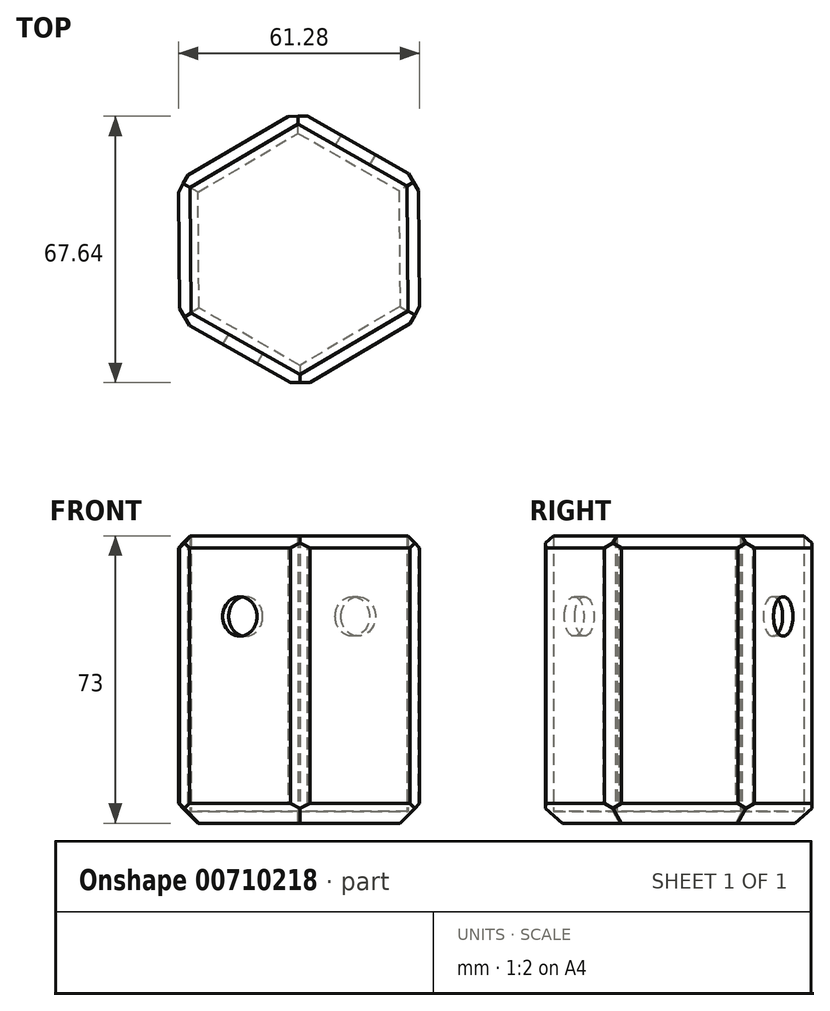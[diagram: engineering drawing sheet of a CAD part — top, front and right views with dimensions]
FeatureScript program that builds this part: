
annotation { "Feature Type Name" : "Feature", "Feature Type Description" : "" }
export const myFeature = defineFeature(function(context is Context, id is Id, definition is map)
    precondition{}
    {
        {
            var Q0;
            Q0=qCreatedBy(makeId("Top.planeOp"),FACE);
            var sketch = newSketch(context, id + "F0", { "sketchPlane" : qUnion([Q0])});
            skCircle(sketch, "E0.cCircle", {"center": v(0, 0) * mm, "radius": 30.52 * mm, "construction": true});
            skLineSegment(sketch, "E0.0", {"start": v(-30.67, 17.36) * mm, "end": v(-0.3, 35.24) * mm});
            skLineSegment(sketch, "E0.1", {"start": v(-0.3, 35.24) * mm, "end": v(30.37, 17.88) * mm});
            skLineSegment(sketch, "E0.2", {"start": v(30.37, 17.88) * mm, "end": v(30.67, -17.36) * mm});
            skLineSegment(sketch, "E0.3", {"start": v(30.67, -17.36) * mm, "end": v(0.3, -35.24) * mm});
            skLineSegment(sketch, "E0.4", {"start": v(0.3, -35.24) * mm, "end": v(-30.37, -17.88) * mm});
            skLineSegment(sketch, "E0.5", {"start": v(-30.37, -17.88) * mm, "end": v(-30.67, 17.36) * mm});
            skPoint(sketch, "E0.0.midPoint", {"position": v(-15.48, 26.3) * mm});
            skSolve(sketch);
        }
        {
            var Q0;
            Q0=makeQuery(id+"F0.imprint","IMPRINT",FACE,{"disambiguationData":[TD([[makeQuery(id+"F0.imprint","IMPRINT",EDGE,{"derivedFrom":sQuery(id+"F0.wireOp",EDGE,"E0.0")}),-1.0]])]});
            extrude(context, id + "F1", {"entities" : qUnion([Q0]), "depth" : 75 * mm, "offsetDistance" : 25 * mm});
        }
        {
            var Q0;
            Q0=makeQuery(id+"F1.opExtrude","CAP_FACE",FACE,{"disambiguationData":[OSD([sQuery(id+"F0.wireOp",EDGE,"E0.0"),sQuery(id+"F0.wireOp",EDGE,"E0.1"),sQuery(id+"F0.wireOp",EDGE,"E0.2"),sQuery(id+"F0.wireOp",EDGE,"E0.3"),sQuery(id+"F0.wireOp",EDGE,"E0.4"),sQuery(id+"F0.wireOp",EDGE,"E0.5")])],"isStart":false});
            shell(context, id + "F2", {"entities" : qUnion([Q0]), "thickness" : 3 * mm});
        }
        {
            var Q0;
            Q0=makeQuery(id+"F1.opExtrude","CAP_FACE",FACE,{"disambiguationData":[OSD([sQuery(id+"F0.wireOp",EDGE,"E0.0"),sQuery(id+"F0.wireOp",EDGE,"E0.1"),sQuery(id+"F0.wireOp",EDGE,"E0.2"),sQuery(id+"F0.wireOp",EDGE,"E0.3"),sQuery(id+"F0.wireOp",EDGE,"E0.4"),sQuery(id+"F0.wireOp",EDGE,"E0.5")])],"isStart":true});
            chamfer(context, id + "F3", {"entities" : qUnion([Q0]), "width" : 5 * mm, "tangentPropagation" : true});
        }
        {
            var Q0;
            Q0=makeQuery(id+"F1.opExtrude","CAP_EDGE",EDGE,{"disambiguationData":[OSD([sQuery(id+"F0.wireOp",EDGE,"E0.4")])],"isStart":false});
            var Q1;
            Q1=makeQuery(id+"F1.opExtrude","CAP_EDGE",EDGE,{"disambiguationData":[OSD([sQuery(id+"F0.wireOp",EDGE,"E0.5")])],"isStart":false});
            var Q2;
            Q2=makeQuery(id+"F1.opExtrude","CAP_EDGE",EDGE,{"disambiguationData":[OSD([sQuery(id+"F0.wireOp",EDGE,"E0.0")])],"isStart":false});
            var Q3;
            Q3=makeQuery(id+"F1.opExtrude","CAP_EDGE",EDGE,{"disambiguationData":[OSD([sQuery(id+"F0.wireOp",EDGE,"E0.1")])],"isStart":false});
            var Q4;
            Q4=makeQuery(id+"F1.opExtrude","CAP_EDGE",EDGE,{"disambiguationData":[OSD([sQuery(id+"F0.wireOp",EDGE,"E0.2")])],"isStart":false});
            var Q5;
            Q5=makeQuery(id+"F1.opExtrude","CAP_EDGE",EDGE,{"disambiguationData":[OSD([sQuery(id+"F0.wireOp",EDGE,"E0.3")])],"isStart":false});
            chamfer(context, id + "F4", {"entities" : qUnion([Q0, Q1, Q2, Q3, Q4, Q5]), "width" : 5 * mm, "tangentPropagation" : true});
        }
        {
            var Q0;
            Q0=makeQuery(id+"F1.opExtrude","SWEPT_FACE",FACE,{"disambiguationData":[OSD([sQuery(id+"F0.wireOp",EDGE,"E0.4")])]});
            var sketch = newSketch(context, id + "F5", { "sketchPlane" : qUnion([Q0])});
            skPoint(sketch, "E1", {"position": v(0, 52.55) * mm});
            skSolve(sketch);
        }
        {
            var Q0;
            Q0=sQuery(id+"F5.wireOp",VERTEX,"E1");
            var Q1;
            Q1=makeQuery(id+"F1.opExtrude","SWEPT_BODY",BODY,{"disambiguationData":[OSD([sQuery(id+"F0.wireOp",EDGE,"E0.0"),sQuery(id+"F0.wireOp",EDGE,"E0.1"),sQuery(id+"F0.wireOp",EDGE,"E0.2"),sQuery(id+"F0.wireOp",EDGE,"E0.3"),sQuery(id+"F0.wireOp",EDGE,"E0.4"),sQuery(id+"F0.wireOp",EDGE,"E0.5")])]});
            hole(context, id + "F6", {"style" : HoleStyle.SIMPLE, "endStyle" : HoleEndStyle.THROUGH, "holeDiameter" : 10 * mm, "majorDiameter" : 5 * mm, "isTappedThrough" : true, "tappedDepth" : 12 * mm, "tapClearance" : 3, "locations" : qUnion([Q0]), "scope" : qUnion([Q1])});
        }
        {
            var Q0;
            Q0=makeQuery(id+"F6.hole-0.boolean.opBoolean","COPY",EDGE,{"derivedFrom":makeQuery(id+"F6.hole-0.opRevolve","SWEPT_EDGE",EDGE,{"disambiguationData":[OSD([sQuery(id+"F6.hole-0.sketch.wireOp",EDGE,"core_line_2"),sQuery(id+"F6.hole-0.sketch.wireOp",EDGE,"core_line_3")])]})});
            var Q1;
            Q1=makeQuery(id+"F6.hole-0.boolean.opBoolean","INTERSECT",EDGE,{"derivedFrom":[makeQuery(id+"F1.opExtrude","SWEPT_FACE",FACE,{"disambiguationData":[OSD([sQuery(id+"F0.wireOp",EDGE,"E0.1")])]}),makeQuery(id+"F6.hole-0.opRevolve","SWEPT_FACE",FACE,{"disambiguationData":[OSD([sQuery(id+"F6.hole-0.sketch.wireOp",EDGE,"core_line_2")])]})]});
            var Q2;
            Q2=makeQuery(id+"F1.opExtrude","SWEPT_EDGE",EDGE,{"disambiguationData":[OSD([sQuery(id+"F0.wireOp",EDGE,"E0.4"),sQuery(id+"F0.wireOp",EDGE,"E0.5")])]});
            var Q3;
            Q3=makeQuery(id+"F1.opExtrude","SWEPT_EDGE",EDGE,{"disambiguationData":[OSD([sQuery(id+"F0.wireOp",EDGE,"E0.0"),sQuery(id+"F0.wireOp",EDGE,"E0.5")])]});
            var Q4;
            Q4=makeQuery(id+"F1.opExtrude","SWEPT_EDGE",EDGE,{"disambiguationData":[OSD([sQuery(id+"F0.wireOp",EDGE,"E0.0"),sQuery(id+"F0.wireOp",EDGE,"E0.1")])]});
            var Q5;
            Q5=makeQuery(id+"F1.opExtrude","SWEPT_EDGE",EDGE,{"disambiguationData":[OSD([sQuery(id+"F0.wireOp",EDGE,"E0.1"),sQuery(id+"F0.wireOp",EDGE,"E0.2")])]});
            var Q6;
            Q6=makeQuery(id+"F1.opExtrude","SWEPT_EDGE",EDGE,{"disambiguationData":[OSD([sQuery(id+"F0.wireOp",EDGE,"E0.2"),sQuery(id+"F0.wireOp",EDGE,"E0.3")])]});
            var Q7;
            Q7=makeQuery(id+"F1.opExtrude","SWEPT_EDGE",EDGE,{"disambiguationData":[OSD([sQuery(id+"F0.wireOp",EDGE,"E0.3"),sQuery(id+"F0.wireOp",EDGE,"E0.4")])]});
            chamfer(context, id + "F7", {"entities" : qUnion([Q0, Q1, Q2, Q3, Q4, Q5, Q6, Q7]), "width" : 5 * mm, "tangentPropagation" : true});
        }
    });
